# Revit family: PRD_AR_FlshCntrlDvcs_F3EUrinalFlushValve_F3EF3001
name_source: partatom
category: Plumbing Fixtures
units: mm (PartAtom-declared; Revit-internal decimal feet)

## family parameters
Cut with Voids When Loaded = No
Enable Cutting in Views = No
Host = Face
Maintain Annotation Orientation = No
OmniClass Number = 23.65.55.14.17
OmniClass Title = Adjusting/Controlling Valves for Liquid Services
Part Type = Normal
Room Calculation Point = No
Round Connector Dimension = Use Diameter
Shared = No

## types (1)
- F3EF3001
    AssetType = Fixed
    BIMObjectName = PRD_AR_FlushControlDevices_F3EUrinalFlushValve_F3EF3001
    BasicColour = chrome-look (glossy)
    BodyMaterial = PRD_AR_ChromatedBrass
    Category = Pr_75_50_46_31, Flush control devices
    CloseOffRating = 0.0 Pa
    Color = chrome-look (glossy)
    DN = 15 mm  [stored 0.0492126 ft]
    Default Elevation = 1200 mm
    DefaultAutomaticHygieneFlush = 24h after the last activity
    Description = F3E urinal flush valve DN 15 for wall mounting, opto-electronically controlled. Control electronics, solenoid valve cartridge, 6 V lithium battery (CR-P2) and sensor in all-metal housing, polished chromium-plated brass. With lockable water volume regulation, urinal connector, flushing pipe and rosette. Activated water hygiene flushing 24 hours after last activation, safety switch-off for continuous reflexion and saving of statistical data. With option for parametrisation and communication via optional, bidirectional remote control.
    DiameterNominal = DN 15
    Export Type to IFC As = IfcValveType
    Features = All-metal housing, polished chromium-plated brass
    Finish = chromed
    Flow = 0.0 L/s
    FlowCoefficient = 0
    FlushingRate = 0.0 L/s
    FunctionalPrinciple = electronic self-closing
    HasIntegralShutOffDevice = TRUE
    HygieneFlushing = yes
    IfcExportAs = IfcValveType
    IfcExportType = FLUSHING
    InletSize = G 1/2 B
    IsHighPressure = FALSE
    Manufacturer = KWC Group Management AG
    ManufacturerName = KWC Group Management AG
    ManufacturerURL = www.kwc-professional.com
    Material = brass
    MaterialFitting = brass-look
    Model = F3EF3001
    ModelNumber = 2030072417
    ModelReference = F3EF3001
    NBSDescription = Flush control devices
    NBSReference = 90-15-35/470
    Name = F3E Urinal Flush Valve F3EF3001
    NominalDepth = 0 mm  [stored 0 ft]
    NominalHeight = 0 mm  [stored 0 ft]
    NominalWidth = 0 mm  [stored 0 ft]
    Parameterization = remote control
    PowerSupplyConnection = Battery 6 V
    ProductInformation = http://pim.kwc.com
    Size = 15 mm  [stored 0.0492126 ft]
    SoundInsulation = no
    Status = New
    SurfaceFinish = chromed
    SurfaceFinishFitting = chromed
    TestPressure = 0.0 Pa
    Type IFC Predefined Type = FLUSHING
    TypeOfBatteries = CR-P2 Lithium battery 6V
    TypeOfFlushingFitting = urinal flush valve
    TypeOfMounting = wall mounting
    TypeOfOperation = sensor operation
    TypeOfPowerSupply = Battery
    TypeOfSensor = opto-electronic sensor
    URL = www.kwc-professional.com
    Uniclass2015Code = Pr_75_50_46_31
    Uniclass2015Title = Flush control devices
    Uniclass2015Version = Products v1.36
    ValveMechanism = OTHER
    ValveOperation = SOLENOID
    ValvePattern = ANGLED_2_PORT
    Version = 1
    WaterConnection = threaded connection (external)
    WorkingPressure = 0.0 Pa

note: [stored X ft] marks values corroborated as IEEE doubles in the binary element streams (Revit-internal decimal feet)

## geometry (parser evidence)
native form markers: Sweep x5
no freeform markers — native parametric forms only
